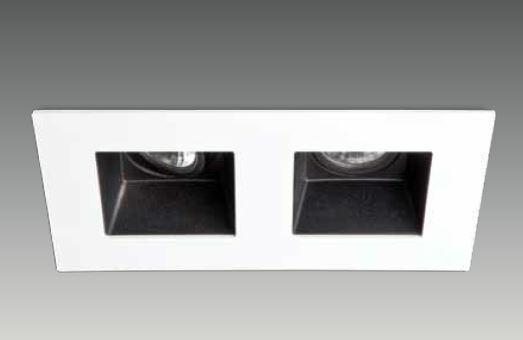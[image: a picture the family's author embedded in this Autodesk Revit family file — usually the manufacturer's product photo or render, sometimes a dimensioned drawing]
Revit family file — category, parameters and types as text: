
# Revit family: DG 2213  SAK
name_source: partatom
category: Lighting Fixtures
revit_build: Autodesk Revit 2017 (Build: 20160225_1515(x64)
units: mm (PartAtom-declared; Revit-internal decimal feet)

## family parameters
Always vertical = Yes
Cut with Voids When Loaded = No
Host = Ceiling
Light Source = Yes
OmniClass Number = 23.80.70.11
OmniClass Title = Luminaries for Internal Lighting
Part Type = Normal
Room Calculation Point = No
Round Connector Dimension = Use Diameter
Shared = No

## types (2) — shared parameters
Apparent Load = 15 VA
Color Filter = 16777215
Dimming Lamp Color Temperature Shift = <None>
Emit Shape Visible in Rendering = Yes
Emit from Rectangle Length = 65 mm  [stored 0.213255 ft]
Emit from Rectangle Width = 65 mm  [stored 0.213255 ft]
Light Source Symbol Length = 3048 mm  [stored 10 ft]
Manufacturer = ARLIGHT
Spot Beam Angle = 35.00°
Spot Field Angle = 90.00°
Tilt Angle = 90.00°
Type Image = DG 2213  SAK.JPG
Wattage Comments = 15W

## type names (no varying parameters)
- DGSAK.2213.15.30.35
- DGSAK.2213.15.40.35

note: [stored X ft] marks values corroborated as IEEE doubles in the binary element streams (Revit-internal decimal feet)

## geometry (parser evidence)
native form markers: Sweep x4
no freeform markers — native parametric forms only
